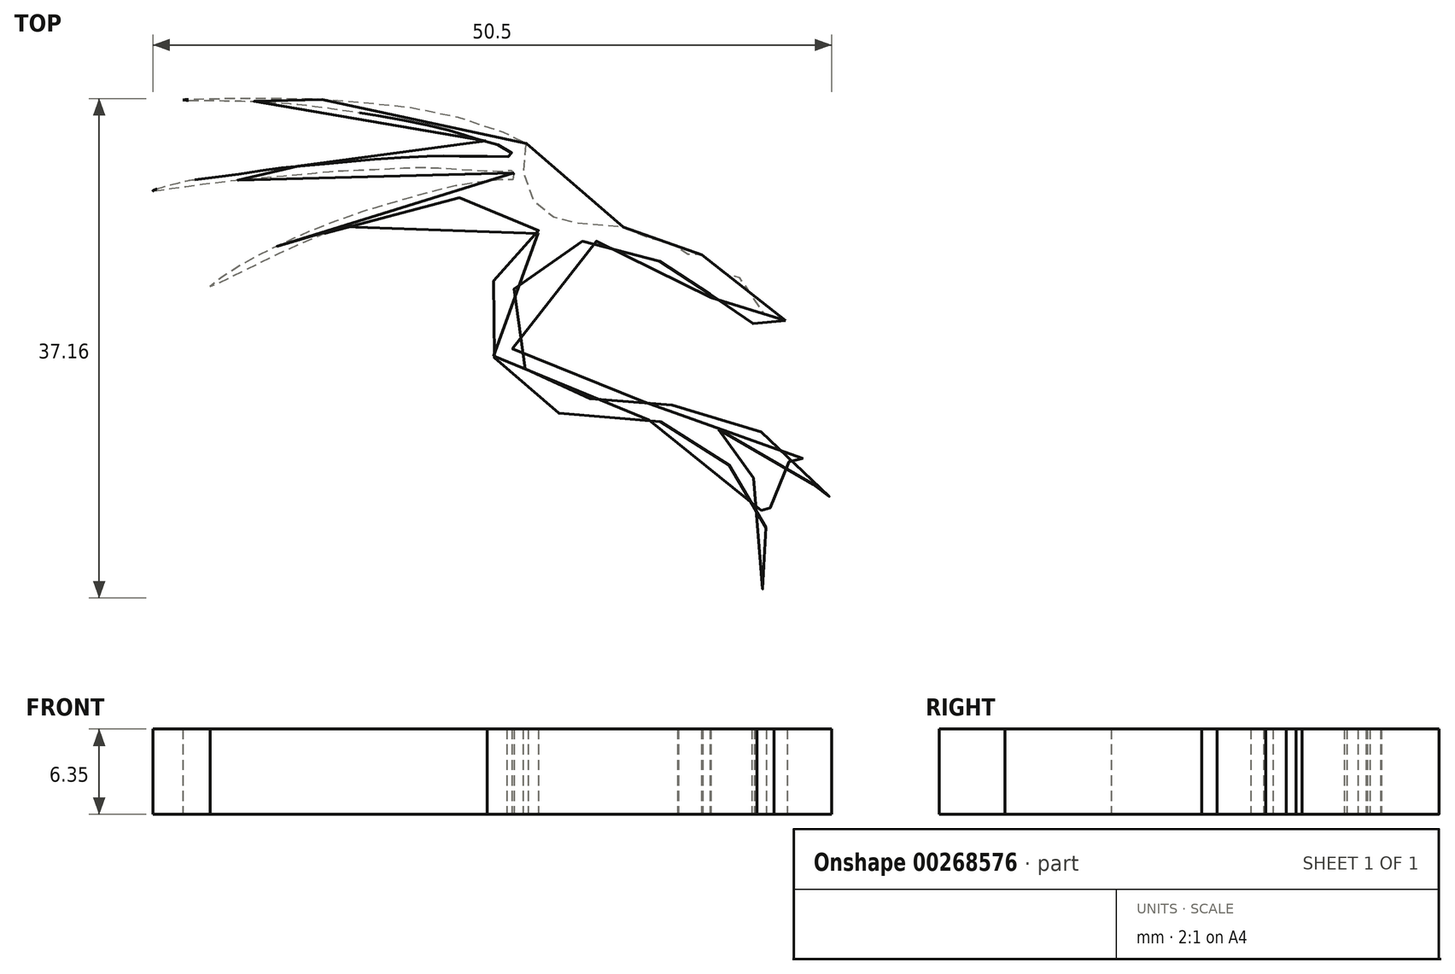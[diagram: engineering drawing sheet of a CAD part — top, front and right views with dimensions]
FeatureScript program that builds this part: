
annotation { "Feature Type Name" : "Feature", "Feature Type Description" : "" }
export const myFeature = defineFeature(function(context is Context, id is Id, definition is map)
    precondition{}
    {
        {
            var Q0;
            Q0=qCreatedBy(makeId("Top.planeOp"),FACE);
            var sketch = newSketch(context, id + "F0", { "sketchPlane" : qUnion([Q0])});
            skFitSpline(sketch, "E0", {"points": [v(-43.11, 37.44) * mm, v(-43.7, 37.4) * mm, v(-44.22, 37.62) * mm, v(-45.05, 38.17) * mm, v(-45.62, 38.72) * mm, v(-45.46, 38.85) * mm, v(-45.5, 39.13) * mm, v(-45.75, 39.31) * mm, v(-46.22, 40.1) * mm, v(-46.76, 41) * mm, v(-46.87, 41.08) * mm, v(-47.23, 41.02) * mm, v(-47.85, 41.02) * mm, v(-49.36, 42.61) * mm, v(-49.39, 42.57) * mm, v(-49.27, 41.67) * mm, v(-49.37, 41.64) * mm, v(-50.32, 42.3) * mm, v(-51.07, 43.24) * mm, v(-51.08, 43.35) * mm, v(-51.14, 43.29) * mm, v(-51.1, 42.64) * mm, v(-51.97, 43.03) * mm, v(-52.26, 43.23) * mm, v(-52.66, 43.77) * mm, v(-52.7, 43.77) * mm, v(-52.76, 43.33) * mm, v(-52.89, 43.4) * mm, v(-53.96, 43.85) * mm, v(-54.82, 44.26) * mm, v(-56.42, 44.6) * mm, v(-59.06, 44.7) * mm, v(-59.25, 44.72) * mm, v(-59.98, 44.97) * mm, v(-60.8, 45.32) * mm, v(-61.43, 45.84) * mm, v(-61.94, 46.5) * mm, v(-62.41, 47.54) * mm, v(-62.63, 48.74) * mm, v(-62.64, 49.6) * mm, v(-62.37, 50.66) * mm, v(-62.27, 50.71) * mm, v(-62.42, 50.8) * mm, v(-64.32, 51.51) * mm, v(-66.8, 52.37) * mm, v(-70.04, 53.12) * mm, v(-72.22, 53.42) * mm, v(-75.14, 53.7) * mm, v(-77.16, 53.88) * mm, v(-78.92, 53.92) * mm, v(-82.1, 53.95) * mm, v(-84.53, 53.95) * mm, v(-85.46, 53.95) * mm, v(-87.95, 53.86) * mm, v(-87.8, 53.84) * mm, v(-87.03, 53.83) * mm, v(-83.74, 53.79) * mm, v(-81.71, 53.7) * mm, v(-78.96, 53.49) * mm, v(-75.84, 53.08) * mm, v(-73.66, 52.73) * mm, v(-69.58, 51.95) * mm, v(-67.14, 51.29) * mm, v(-66.06, 50.95) * mm, v(-63.52, 50.02) * mm, v(-63.6, 49.65) * mm, v(-63.73, 49.63) * mm, v(-67.62, 49.67) * mm, v(-68.99, 49.69) * mm, v(-73.16, 49.48) * mm, v(-76.77, 49.15) * mm, v(-80.65, 48.8) * mm, v(-83.76, 48.35) * mm, v(-87.04, 47.92) * mm, v(-88.58, 47.6) * mm, v(-90.18, 47.11) * mm, v(-90.04, 47.11) * mm, v(-88.8, 47.27) * mm, v(-84.8, 47.8) * mm, v(-79.09, 48.33) * mm, v(-76.36, 48.58) * mm, v(-72.92, 48.72) * mm, v(-69.55, 48.83) * mm, v(-63.82, 48.58) * mm, v(-63.42, 48.59) * mm, v(-63.33, 48.1) * mm, v(-63.36, 47.96) * mm, v(-63.86, 47.93) * mm, v(-67.12, 47.57) * mm, v(-70.37, 46.78) * mm, v(-75.28, 45.31) * mm, v(-79.19, 43.79) * mm, v(-81.45, 42.73) * mm, v(-84.1, 41.3) * mm, v(-85.92, 39.97) * mm, v(-85.8, 39.99) * mm, v(-84.72, 40.52) * mm, v(-83.23, 41.25) * mm, v(-80.78, 42.45) * mm, v(-76.9, 44.12) * mm, v(-74.8, 44.79) * mm, v(-70.01, 46.09) * mm, v(-67.06, 46.62) * mm, v(-63.16, 46.9) * mm, v(-62.74, 46.72) * mm, v(-62.45, 46.23) * mm, v(-62.09, 45.32) * mm, v(-61.49, 44.06) * mm, v(-61.63, 43.84) * mm, v(-62.24, 43.4) * mm, v(-63.41, 42.57) * mm, v(-63.98, 41.88) * mm, v(-64.4, 41.31) * mm, v(-64.75, 40.6) * mm, v(-64.98, 39.88) * mm, v(-65.12, 39.1) * mm, v(-65.24, 37.7) * mm, v(-65.33, 36.92) * mm, v(-65.1, 35.63) * mm, v(-64.65, 34.41) * mm, v(-64.09, 33.51) * mm, v(-63.34, 32.57) * mm, v(-61.93, 31.35) * mm, v(-60.74, 30.8) * mm, v(-59.54, 30.42) * mm, v(-58.32, 30.26) * mm, v(-56.68, 30.21) * mm, v(-54, 30.14) * mm, v(-52.25, 29.86) * mm, v(-51.54, 29.58) * mm, v(-50.55, 29.14) * mm, v(-49.02, 28.36) * mm, v(-48.3, 27.72) * mm, v(-47.37, 26.77) * mm, v(-46.64, 25.84) * mm, v(-46.33, 25.34) * mm, v(-45.62, 24.49) * mm, v(-45.43, 24.17) * mm, v(-44.88, 23.24) * mm, v(-44.6, 22.12) * mm, v(-44.53, 20.7) * mm, v(-44.63, 18.98) * mm, v(-44.91, 17.86) * mm, v(-45.26, 16.8) * mm, v(-45.12, 16.98) * mm, v(-44.53, 18.15) * mm, v(-43.98, 21.23) * mm, v(-44.27, 23.56) * mm, v(-45.24, 25.3) * mm, v(-46.6, 27.36) * mm, v(-47.9, 28.62) * mm, v(-48.85, 29.3) * mm, v(-49.3, 29.57) * mm, v(-49.05, 29.54) * mm, v(-46.43, 28.85) * mm, v(-43.46, 27.28) * mm, v(-42.3, 26.52) * mm, v(-41.52, 25.7) * mm, v(-40.74, 24.9) * mm, v(-40.07, 23.58) * mm, v(-39.94, 21.69) * mm, v(-39.86, 21.88) * mm, v(-39.68, 23.47) * mm, v(-39.97, 24.6) * mm, v(-40.77, 26.14) * mm, v(-41.91, 27.25) * mm, v(-42.76, 27.93) * mm, v(-44.56, 28.96) * mm, v(-46.15, 29.78) * mm, v(-48.5, 30.53) * mm, v(-49.47, 30.8) * mm, v(-50.23, 30.97) * mm, v(-51.6, 31.17) * mm, v(-52.61, 31.34) * mm, v(-53.44, 31.4) * mm, v(-54.65, 31.5) * mm, v(-55.8, 31.58) * mm, v(-57.4, 31.6) * mm, v(-58.67, 31.72) * mm, v(-59.67, 31.9) * mm, v(-60.42, 32.22) * mm, v(-61.22, 32.54) * mm, v(-61.84, 33.16) * mm, v(-62.58, 33.94) * mm, v(-63.24, 34.92) * mm, v(-63.63, 35.98) * mm, v(-63.84, 37.42) * mm, v(-63.61, 38.75) * mm, v(-63.27, 39.9) * mm, v(-62.71, 40.94) * mm, v(-61.53, 42.2) * mm, v(-60.22, 43) * mm, v(-58.9, 43.27) * mm, v(-58, 43.36) * mm, v(-57, 43.35) * mm, v(-55.8, 43.13) * mm, v(-54.86, 42.85) * mm, v(-54, 42.41) * mm, v(-52.52, 41.88) * mm, v(-51.27, 41.37) * mm, v(-50.4, 40.94) * mm, v(-49.47, 40.6) * mm, v(-48.7, 40.28) * mm, v(-48.68, 40.12) * mm, v(-48.73, 39.6) * mm, v(-48.75, 39.43) * mm, v(-48.7, 39.22) * mm, v(-48.47, 38.99) * mm, v(-48.02, 38.73) * mm, v(-47.53, 38.52) * mm, v(-47.02, 38.34) * mm, v(-46.66, 38.1) * mm, v(-46.41, 37.82) * mm, v(-45.64, 37.27) * mm, v(-45.33, 37.1) * mm, v(-45.02, 36.86) * mm, v(-44.74, 36.47) * mm, v(-44.5, 36.32) * mm, v(-44.44, 36.37) * mm, v(-44.15, 36.57) * mm, v(-43.8, 36.83) * mm, v(-43.41, 37.04) * mm, v(-43.02, 37.25) * mm, v(-43.11, 37.44) * mm]});
            skSolve(sketch);
        }
        {
            var Q0;
            Q0 = qSketchRegion(id + "F0", true);
            extrude(context, id + "F1", {"entities" : qUnion([Q0]), "depth" : 6.35 * mm});
        }
    });
